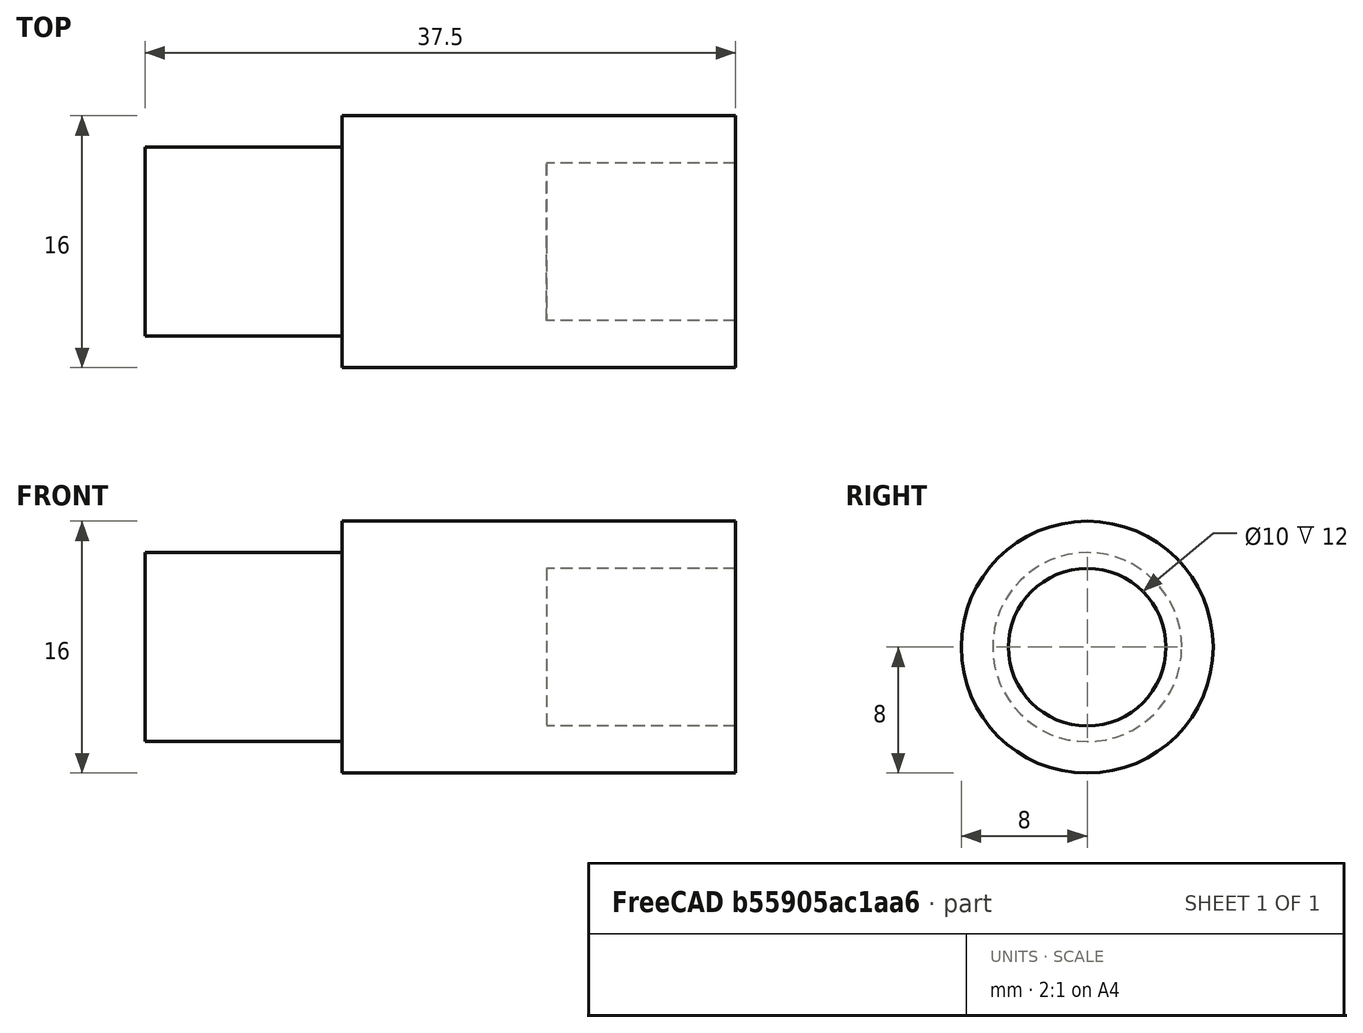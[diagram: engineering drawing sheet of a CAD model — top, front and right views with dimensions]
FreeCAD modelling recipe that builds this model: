
FCSTD DOCUMENT  (FreeCAD 0.16R5750 (Git))
Label: Left-Cover-150-bushing-new
License: CreativeCommons Attribution-ShareAlike
LicenseURL: http://creativecommons.org/licenses/by-sa/4.0/
objects: Sketcher::SketchObject×1, PartDesign::Revolution×1
note: 3 computed .brp shape members not serialized (recipe doc carries the construction recipe); baked Part::Feature solids carry a one-line shape summary decoded from their .brp

FEATURE [Sketcher::SketchObject] Sketch
  Placement = pos=(0,0,0) rot=(1,0,0;1.5708rad)
  sketch-geometry (8):
    g0: LineSegment StartX=13 StartY=0 StartZ=0 EndX=-12.5 EndY=0 EndZ=0
    g1: LineSegment StartX=-12.5 StartY=0 StartZ=0 EndX=-12.5 EndY=6 EndZ=0
    g2: LineSegment StartX=-12.5 StartY=6 StartZ=0 EndX=0 EndY=6 EndZ=0
    g3: LineSegment StartX=0 StartY=6 StartZ=0 EndX=0 EndY=8 EndZ=0
    g4: LineSegment StartX=0 StartY=8 StartZ=0 EndX=25 EndY=8 EndZ=0
    g5: LineSegment StartX=25 StartY=8 StartZ=0 EndX=25 EndY=5 EndZ=0
    g6: LineSegment StartX=25 StartY=5 StartZ=0 EndX=13 EndY=5 EndZ=0
    g7: LineSegment StartX=13 StartY=5 StartZ=0 EndX=13 EndY=0 EndZ=0
  constraints (24):
    c: Coincident(g0,g1)
    c: Coincident(g1,g2)
    c: Coincident(g2,g3)
    c: Coincident(g4,g5)
    c: Coincident(g5,g6)
    c: Coincident(g6,g7)
    c: Coincident(g0,g7)
    c: Vertical(g7)
    c: Coincident(g3,g4)
    c: Horizontal(g4)
    c: Horizontal(g6)
    c: Vertical(g5)
    c: DistanceX(g0,g5) = 12
    c: Vertical(g3)
    c: DistanceY(g0,g5) = 5
    c: Horizontal(g0)
    c: Vertical(g1)
    c: Horizontal(g2)
    c: DistanceX(g1,g2) = 12.5
    c: DistanceY(g4) = 8
    c: DistanceY(g-1,g1) = 6
    c: PointOnObject(g2,g-2)
    c: PointOnObject(g0,g-1)
    c: DistanceX(g1,g4) = 37.5
FEATURE [PartDesign::Revolution] Revolution
  Angle = 360
  Axis = (1,0,0)
  Base = (0,0,0)
  Placement = pos=(0,0,0) rot=(1,0,0;1.5708rad)
  ReferenceAxis = -> Sketch [H_Axis]
  Sketch = -> Sketch
